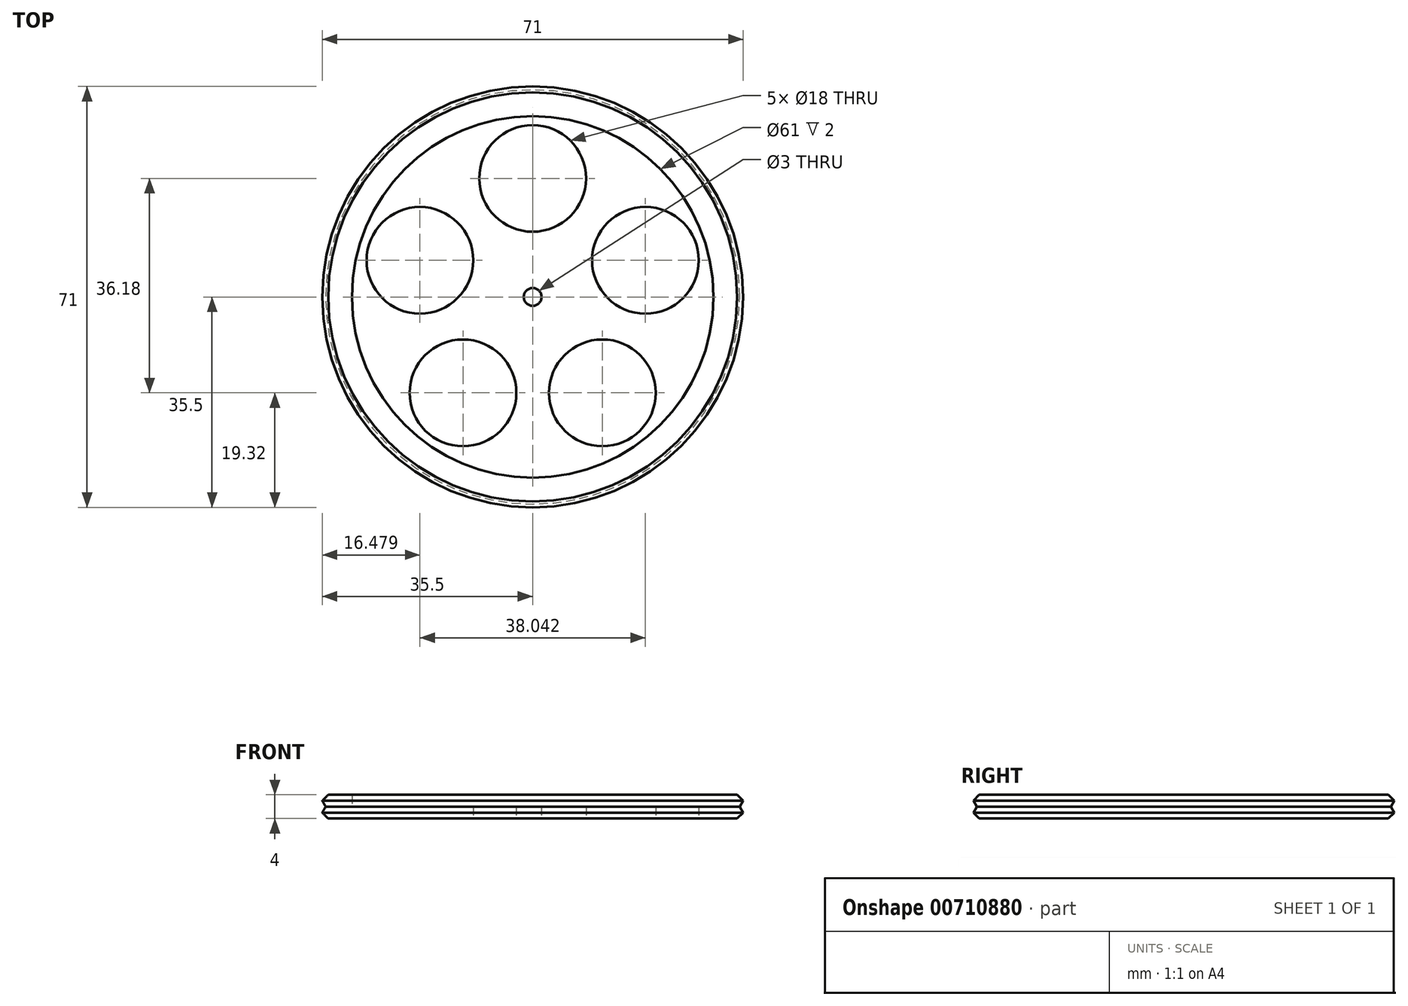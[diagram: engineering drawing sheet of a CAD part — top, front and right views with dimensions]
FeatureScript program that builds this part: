
annotation { "Feature Type Name" : "Feature", "Feature Type Description" : "" }
export const myFeature = defineFeature(function(context is Context, id is Id, definition is map)
    precondition{}
    {
        {
            var Q0;
            Q0=qCreatedBy(makeId("Top.planeOp"),FACE);
            var sketch = newSketch(context, id + "F0", { "sketchPlane" : qUnion([Q0])});
            skCircle(sketch, "E0", {"center": v(0, 0) * mm, "radius": 35.5 * mm});
            skCircle(sketch, "E1", {"center": v(0, 20) * mm, "radius": 9 * mm});
            skCircle(sketch, "E2.1.0", {"center": v(-19.02, 6.18) * mm, "radius": 9 * mm});
            skCircle(sketch, "E2.2.0", {"center": v(-11.76, -16.18) * mm, "radius": 9 * mm});
            skCircle(sketch, "E2.3.0", {"center": v(11.76, -16.18) * mm, "radius": 9 * mm});
            skCircle(sketch, "E2.4.0", {"center": v(19.02, 6.18) * mm, "radius": 9 * mm});
            skLineSegment(sketch, "E3", {"start": v(0, 0) * mm, "end": v(0, 47.73) * mm, "construction": true});
            skPoint(sketch, "E4", {"position": v(0, 35.5) * mm});
            skCircle(sketch, "E5", {"center": v(0, 0) * mm, "radius": 1.5 * mm});
            skSolve(sketch);
        }
        {
            var Q0;
            Q0=qCreatedBy(makeId("Right.planeOp"),FACE);
            var sketch = newSketch(context, id + "F1", { "sketchPlane" : qUnion([Q0])});
            skLineSegment(sketch, "E6", {"start": v(0, 0) * mm, "end": v(35.5, 0) * mm});
            skLineSegment(sketch, "E7", {"start": v(35.5, 0) * mm, "end": v(35.5, 1) * mm});
            skLineSegment(sketch, "E8", {"start": v(35.5, 1) * mm, "end": v(34.92, 2) * mm});
            skLineSegment(sketch, "E9", {"start": v(34.92, 2) * mm, "end": v(35.5, 3) * mm});
            skLineSegment(sketch, "E10", {"start": v(35.5, 3) * mm, "end": v(35.5, 4) * mm});
            skLineSegment(sketch, "E11", {"start": v(35.5, 4) * mm, "end": v(30.5, 4) * mm});
            skLineSegment(sketch, "E12", {"start": v(30.5, 4) * mm, "end": v(30.5, 2) * mm});
            skLineSegment(sketch, "E13", {"start": v(30.5, 2) * mm, "end": v(0, 2) * mm});
            skLineSegment(sketch, "E14", {"start": v(0, 2) * mm, "end": v(0, 0) * mm});
            skLineSegment(sketch, "E15", {"start": v(0, 0) * mm, "end": v(0, 23.42) * mm, "construction": true});
            skSolve(sketch);
        }
        {
            var Q0;
            Q0=makeQuery(id+"F1.imprint","IMPRINT",FACE,{"disambiguationData":[TD([[makeQuery(id+"F1.imprint","IMPRINT",EDGE,{"derivedFrom":sQuery(id+"F1.wireOp",EDGE,"E6")}),1.0]])]});
            var Q1;
            Q1=sQuery(id+"F1.wireOp",EDGE,"E15");
            revolve(context, id + "F2", {"surfaceOperationType" : NewSurfaceOperationType.NEW, "entities" : qUnion([Q0]), "axis" : qUnion([Q1]), "revolveType" : RevolveType.FULL});
        }
        {
            var Q0;
            Q0=makeQuery(id+"F0.imprint","IMPRINT",FACE,{"disambiguationData":[TD([[makeQuery(id+"F0.imprint","IMPRINT",EDGE,{"derivedFrom":sQuery(id+"F0.wireOp",EDGE,"E2.3.0")}),1.0]])]});
            var Q1;
            Q1=makeQuery(id+"F0.imprint","IMPRINT",FACE,{"disambiguationData":[TD([[makeQuery(id+"F0.imprint","IMPRINT",EDGE,{"derivedFrom":sQuery(id+"F0.wireOp",EDGE,"E2.2.0")}),1.0]])]});
            var Q2;
            Q2=makeQuery(id+"F0.imprint","IMPRINT",FACE,{"disambiguationData":[TD([[makeQuery(id+"F0.imprint","IMPRINT",EDGE,{"derivedFrom":sQuery(id+"F0.wireOp",EDGE,"E2.1.0")}),1.0]])]});
            var Q3;
            Q3=makeQuery(id+"F0.imprint","IMPRINT",FACE,{"disambiguationData":[TD([[makeQuery(id+"F0.imprint","IMPRINT",EDGE,{"derivedFrom":sQuery(id+"F0.wireOp",EDGE,"E1")}),1.0]])]});
            var Q4;
            Q4=makeQuery(id+"F0.imprint","IMPRINT",FACE,{"disambiguationData":[TD([[makeQuery(id+"F0.imprint","IMPRINT",EDGE,{"derivedFrom":sQuery(id+"F0.wireOp",EDGE,"E2.4.0")}),1.0]])]});
            var Q5;
            Q5=makeQuery(id+"F0.imprint","IMPRINT",FACE,{"disambiguationData":[TD([[makeQuery(id+"F0.imprint","IMPRINT",EDGE,{"derivedFrom":sQuery(id+"F0.wireOp",EDGE,"E5")}),1.0]])]});
            extrude(context, id + "F3", {"entities" : qUnion([Q0, Q1, Q2, Q3, Q4, Q5]), "operationType" : NewBodyOperationType.REMOVE, "depth" : 25 * mm, "offsetDistance" : 25 * mm});
        }
        {
            var Q0;
            Q0=makeQuery(id+"F2.opRevolve","SWEPT_EDGE",EDGE,{"disambiguationData":[OSD([sQuery(id+"F1.wireOp",EDGE,"E10"),sQuery(id+"F1.wireOp",EDGE,"E11")])]});
            var Q1;
            Q1=makeQuery(id+"F2.opRevolve","SWEPT_EDGE",EDGE,{"disambiguationData":[OSD([sQuery(id+"F1.wireOp",EDGE,"E6"),sQuery(id+"F1.wireOp",EDGE,"E7")])]});
            chamfer(context, id + "F4", {"entities" : qUnion([Q0, Q1]), "width" : 1 * mm, "tangentPropagation" : true});
        }
    });
